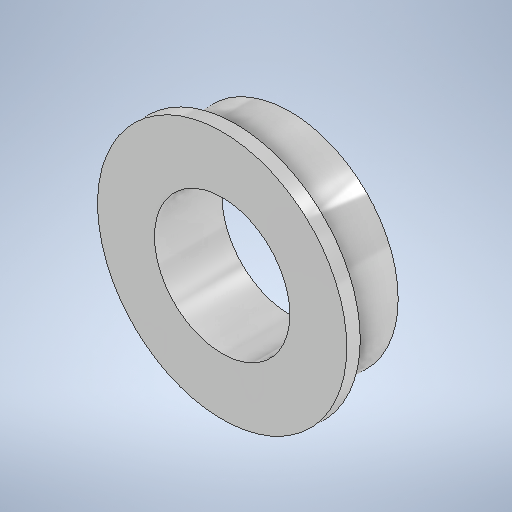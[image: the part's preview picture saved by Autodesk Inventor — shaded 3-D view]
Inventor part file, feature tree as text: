
AUTODESK INVENTOR PART (.ipt)
format: ipt  version: 2025.2 (Build 292293000, 293)  size: 260,608 bytes
history: native  units: mm
features: extrude x3, sketch x3
ambient origin geometry x8: Origin, YZ Plane, XZ Plane, XY Plane, X Axis, Y Axis, Z Axis, Center Point
bodies: Solid1 (feature_tree)
feature tree (6):
  extrude  "Extrusion1"  Depth=2.0mm TaperAngle=0.0deg
  extrude  "Extrusion2"  Depth=9.2mm
  extrude  "Extrusion3"  Depth=0.5mm
  sketch  "Sketch1"  dims[d0=8.0mm d1=2.0mm d2=0.0mm]
  sketch  "Sketch2"  dims[d3=5.0mm d4=9.2mm]
  sketch  "Sketch3"  dims[d5=0.5mm d6=0.0mm d7=5.0mm d8=9.0mm d9=0.0mm]
